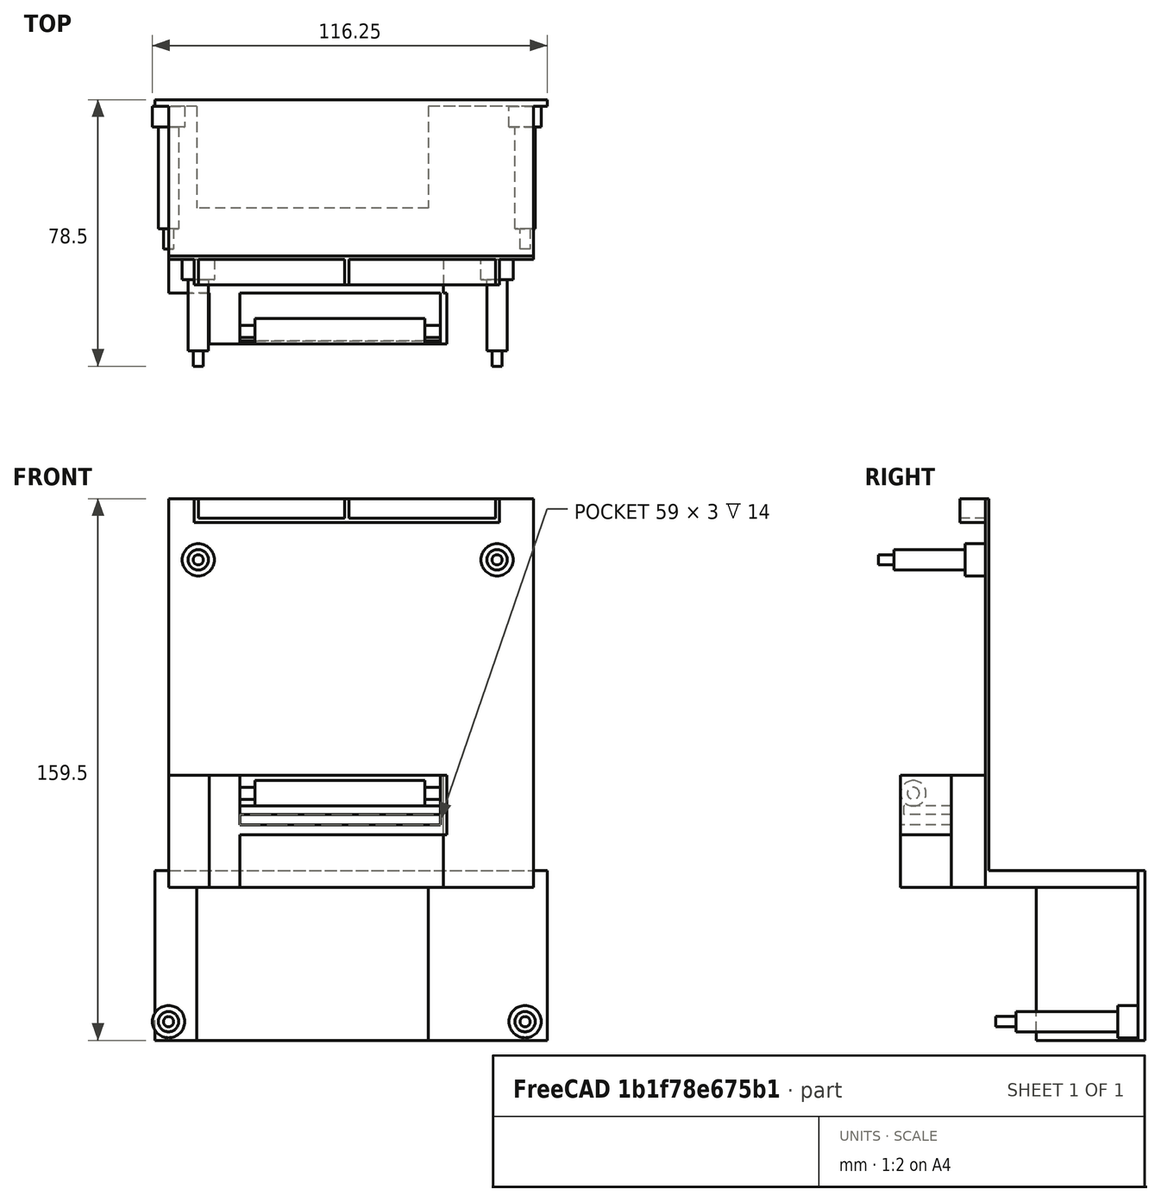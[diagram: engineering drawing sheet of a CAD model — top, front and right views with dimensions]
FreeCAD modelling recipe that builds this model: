
FCSTD DOCUMENT  (FreeCAD 1.0R39285 (Git))
Label: Modified-Printer-approximation
License: All rights reserved
LicenseURL: https://en.wikipedia.org/wiki/All_rights_reserved
objects: Sketcher::SketchObject×17, PartDesign::Pad×17, Part::Helix×2, App::Link×2, PartDesign::Body×1
note: 88 computed .brp shape members not serialized (recipe doc carries the construction recipe); baked Part::Feature solids carry a one-line shape summary decoded from their .brp

FEATURE [Sketcher::SketchObject] Sketch004
  ArcFitTolerance = 1e-06
  AttachmentSupport = -> [XZ_Plane002]
  FullyConstrained = true
  MakeInternals = false
  MapMode = 5
  Placement = pos=(0,0,0) rot=(1,0,0;1.5708rad)
  sketch-geometry (4):
    g0: LineSegment StartX=0 StartY=0 StartZ=0 EndX=0 EndY=-114.5 EndZ=0
    g1: LineSegment StartX=0 StartY=-114.5 StartZ=0 EndX=107.5 EndY=-114.5 EndZ=0
    g2: LineSegment StartX=107.5 StartY=-114.5 StartZ=0 EndX=107.5 EndY=0 EndZ=0
    g3: LineSegment StartX=107.5 StartY=0 StartZ=0 EndX=0 EndY=0 EndZ=0
  constraints (11):
    c: Coincident(g0,g1)
    c: Coincident(g1,g2)
    c: Coincident(g2,g3)
    c: Coincident(g3,g0)
    c: Vertical(g0)
    c: Vertical(g2)
    c: Horizontal(g1)
    c: Horizontal(g3)
    c: Distance(g0,g2) = 107.5
    c: Distance(g1,g3) = 114.5
    c: Coincident(g0,g-1)
FEATURE [PartDesign::Pad] Pad
  Direction = (0,-1,2e-16)
  Length = 1
  Length2 = 10
  Placement = pos=(0,0,0) rot=(1,0,0;1.5708rad)
  Profile = -> Sketch004
  ReferenceAxis = -> Sketch004 [N_Axis]
  Refine = true
  Reversed = true
  Suppressed = false
  Type = 0
FEATURE [Sketcher::SketchObject] Sketch
  ArcFitTolerance = 1e-06
  AttachmentSupport = -> [Pad]
  ExternalGeometry = -> [Pad]
  FullyConstrained = true
  MakeInternals = false
  MapMode = 5
  Placement = pos=(0,-1.27e-14,0) rot=(1,0,0;1.5708rad)
  sketch-geometry (15):
    g0: LineSegment StartX=97.5 StartY=0 StartZ=0 EndX=96.25 EndY=0 EndZ=0
    g1: LineSegment StartX=96.25 StartY=0 StartZ=0 EndX=96.25 EndY=-5.75 EndZ=0
    g2: LineSegment StartX=97.5 StartY=-7 StartZ=0 EndX=97.5 EndY=0 EndZ=0
    g3: LineSegment StartX=96.25 StartY=-5.75 StartZ=0 EndX=53.125 EndY=-5.75 EndZ=0
    g4: LineSegment StartX=7.5 StartY=-7 StartZ=0 EndX=97.5 EndY=-7 EndZ=0
    g5: LineSegment StartX=7.5 StartY=-7 StartZ=0 EndX=7.5 EndY=0 EndZ=0
    g6: LineSegment StartX=8.75 StartY=-5.75 StartZ=0 EndX=8.75 EndY=0 EndZ=0
    g7: LineSegment StartX=8.75 StartY=0 StartZ=0 EndX=7.5 EndY=0 EndZ=0
    g8: LineSegment StartX=53.125 StartY=-5.75 StartZ=0 EndX=53.125 EndY=0 EndZ=0
    g9: LineSegment StartX=53.125 StartY=0 StartZ=0 EndX=51.875 EndY=0 EndZ=0
    g10: LineSegment StartX=51.875 StartY=0 StartZ=0 EndX=51.875 EndY=-5.75 EndZ=0
    g11: LineSegment StartX=51.875 StartY=-5.75 StartZ=0 EndX=8.75 EndY=-5.75 EndZ=0
    g12: LineSegment [constr] StartX=53.125 StartY=-5.75 StartZ=0 EndX=53.125 EndY=-7 EndZ=0
    g13: LineSegment [constr] StartX=0 StartY=0 StartZ=0 EndX=7.5 EndY=0 EndZ=0
    g14: LineSegment [constr] StartX=97.5 StartY=0 StartZ=0 EndX=107.5 EndY=0 EndZ=0
  constraints (44):
    c: Coincident(g0,g1)
    c: Coincident(g2,g0)
    c: Horizontal(g0)
    c: Vertical(g1)
    c: Vertical(g2)
    c: Distance(g1,g2) = 1.25
    c: Distance(g0,g2) = 7
    c: PointOnObject(g0,g-1)
    c: Horizontal(g3)
    c: Horizontal(g4)
    c: Distance(g4,g4) = 90
    c: Coincident(g1,g3)
    c: Coincident(g2,g4)
    c: Coincident(g5,g4)
    c: PointOnObject(g5,g-1)
    c: Vertical(g5)
    c: Coincident(g6,g11)
    c: PointOnObject(g6,g-1)
    c: Vertical(g6)
    c: Coincident(g7,g6)
    c: Coincident(g7,g5)
    c: Equal(g7,g0)
    c: Coincident(g8,g9)
    c: Coincident(g9,g10)
    c: Horizontal(g9)
    c: Vertical(g8)
    c: Vertical(g10)
    c: PointOnObject(g8,g-1)
    c: Coincident(g10,g11)
    c: Coincident(g3,g8)
    c: Horizontal(g10,g3)
    c: Equal(g9,g7)
    c: Horizontal(g11)
    c: Vertical(g12)
    c: PointOnObject(g12,g4)
    c: Equal(g12,g9)
    c: Coincident(g3,g12)
    c: Equal(g11,g3)
    c: Coincident(g13,g-1)
    c: Coincident(g13,g5)
    c: DistanceX(g13,g13) = 7.5
    c: Coincident(g14,g0)
    c: Coincident(g14,g-3)
    c: DistanceX(g14,g14) = 10
FEATURE [PartDesign::Pad] Pad001
  BaseFeature = -> Pad
  Direction = (0,-1,2e-16)
  Length = 7.5
  Length2 = 10
  Placement = pos=(0,0,0) rot=(1,0,0;1.5708rad)
  Profile = -> Sketch
  ReferenceAxis = -> Sketch [N_Axis]
  Refine = true
  Suppressed = false
  Type = 0
FEATURE [Sketcher::SketchObject] Sketch005
  ArcFitTolerance = 1e-06
  AttachmentSupport = -> [Pad001]
  ExternalGeometry = -> [Pad001]
  FullyConstrained = true
  MakeInternals = false
  MapMode = 5
  Placement = pos=(0,-1.27e-14,0) rot=(1,0,0;1.5708rad)
  sketch-geometry (4):
    g0: Circle CenterX=8.75 CenterY=-18 CenterZ=0 NormalX=0 NormalY=0 NormalZ=1 AngleXU=0 Radius=4.75
    g1: Circle CenterX=96.75 CenterY=-18 CenterZ=0 NormalX=0 NormalY=0 NormalZ=1 AngleXU=0 Radius=4.75
    g2: LineSegment [constr] StartX=4 StartY=-18 StartZ=0 EndX=0 EndY=-18 EndZ=0
    g3: LineSegment [constr] StartX=101.5 StartY=-18 StartZ=0 EndX=107.5 EndY=-18 EndZ=0
  constraints (14):
    c: Equal(g0,g1)
    c: Horizontal(g1,g0)
    c: Diameter(g0) = 9.5
    c: PointOnObject(g2,g0)
    c: PointOnObject(g2,g-3)
    c: Horizontal(g2)
    c: Horizontal(g2,g0)
    c: PointOnObject(g3,g1)
    c: PointOnObject(g3,g-4)
    c: Horizontal(g3)
    c: Horizontal(g3,g1)
    c: DistanceX(g3,g3) = 6
    c: DistanceX(g2,g2) = 4
    c: DistanceY(g0,g-1) = 18
FEATURE [PartDesign::Pad] Pad002
  BaseFeature = -> Pad001
  Direction = (0,-1,2e-16)
  Length = 6
  Length2 = 10
  Placement = pos=(0,0,0) rot=(1,0,0;1.5708rad)
  Profile = -> Sketch005
  ReferenceAxis = -> Sketch005 [N_Axis]
  Refine = true
  Suppressed = false
  Type = 0
FEATURE [Sketcher::SketchObject] Sketch006
  ArcFitTolerance = 1e-06
  AttachmentSupport = -> [Pad002]
  ExternalGeometry = -> [Pad002]
  FullyConstrained = true
  MakeInternals = false
  MapMode = 5
  Placement = pos=(0,-6,0) rot=(1,0,0;1.5708rad)
  sketch-geometry (2):
    g0: Circle CenterX=8.75 CenterY=-18 CenterZ=0 NormalX=0 NormalY=0 NormalZ=1 AngleXU=0 Radius=3
    g1: Circle CenterX=96.75 CenterY=-18 CenterZ=0 NormalX=0 NormalY=0 NormalZ=1 AngleXU=0 Radius=3
  constraints (4):
    c: Coincident(g0,g-3)
    c: Coincident(g1,g-4)
    c: Equal(g0,g1)
    c: Diameter(g0) = 6
FEATURE [PartDesign::Pad] Pad003
  BaseFeature = -> Pad002
  Direction = (0,-1,2e-16)
  Length = 21
  Length2 = 10
  Placement = pos=(0,0,0) rot=(1,0,0;1.5708rad)
  Profile = -> Sketch006
  ReferenceAxis = -> Sketch006 [N_Axis]
  Refine = true
  Suppressed = false
  Type = 0
FEATURE [Sketcher::SketchObject] Sketch007
  ArcFitTolerance = 1e-06
  AttachmentSupport = -> [Pad003]
  ExternalGeometry = -> [Pad003]
  FullyConstrained = true
  MakeInternals = false
  MapMode = 5
  Placement = pos=(0,-27,0) rot=(1,0,0;1.5708rad)
  sketch-geometry (2):
    g0: Circle CenterX=8.75 CenterY=-18 CenterZ=0 NormalX=0 NormalY=0 NormalZ=1 AngleXU=0 Radius=1.5
    g1: Circle CenterX=96.75 CenterY=-18 CenterZ=0 NormalX=0 NormalY=0 NormalZ=1 AngleXU=0 Radius=1.5
  constraints (4):
    c: Diameter(g0) = 3
    c: Coincident(g0,g-3)
    c: Coincident(g1,g-4)
    c: Equal(g1,g0)
FEATURE [PartDesign::Pad] Pad004
  BaseFeature = -> Pad003
  Direction = (0,-1,2e-16)
  Length = 4.5
  Length2 = 10
  Placement = pos=(0,0,0) rot=(1,0,0;1.5708rad)
  Profile = -> Sketch007
  ReferenceAxis = -> Sketch007 [N_Axis]
  Refine = true
  Suppressed = false
  Type = 0
FEATURE [Part::Helix] Helix002
  Angle = 0
  AttacherType = Attacher::AttachEngine3D
  Height = 4.5
  Length = 42.6496
  LocalCoord = 0
  Pitch = 1
  Placement = pos=(8.75,-27,-18) rot=(1,0,0;1.5708rad)
  Radius = 1.5
  SegmentLength = 0
  Style = 1
FEATURE [App::Link] Link  label="Helix003"
  LinkPlacement = pos=(96.75,-27,-18) rot=(1,0,0;1.5708rad)
  LinkedObject = -> Helix002
  Placement = pos=(96.75,-27,-18) rot=(1,0,0;1.5708rad)
FEATURE [Sketcher::SketchObject] Sketch008
  ArcFitTolerance = 1e-06
  AttachmentSupport = -> [Pad004]
  ExternalGeometry = -> [Pad004]
  FullyConstrained = true
  MakeInternals = false
  MapMode = 5
  Placement = pos=(0,-1.27e-14,0) rot=(1,0,0;1.5708rad)
  sketch-geometry (4):
    g0: LineSegment StartX=0 StartY=-114.5 StartZ=0 EndX=81 EndY=-114.5 EndZ=0
    g1: LineSegment StartX=81 StartY=-114.5 StartZ=0 EndX=81 EndY=-81.5 EndZ=0
    g2: LineSegment StartX=81 StartY=-81.5 StartZ=0 EndX=0 EndY=-81.5 EndZ=0
    g3: LineSegment StartX=0 StartY=-81.5 StartZ=0 EndX=0 EndY=-114.5 EndZ=0
  constraints (11):
    c: Coincident(g0,g1)
    c: Coincident(g1,g2)
    c: Coincident(g2,g3)
    c: Coincident(g3,g0)
    c: Horizontal(g0)
    c: Horizontal(g2)
    c: Vertical(g1)
    c: Vertical(g3)
    c: Distance(g1,g3) = 81
    c: Distance(g0,g2) = 33
    c: Coincident(g0,g-3)
FEATURE [PartDesign::Pad] Pad005
  BaseFeature = -> Pad004
  Direction = (0,-1,2e-16)
  Length = 10
  Length2 = 10
  Placement = pos=(0,0,0) rot=(1,0,0;1.5708rad)
  Profile = -> Sketch008
  ReferenceAxis = -> Sketch008 [N_Axis]
  Refine = true
  Suppressed = false
  Type = 0
FEATURE [Sketcher::SketchObject] Sketch009
  ArcFitTolerance = 1e-06
  AttachmentSupport = -> [Pad005]
  ExternalGeometry = -> [Pad005]
  FullyConstrained = true
  MakeInternals = false
  MapMode = 5
  Placement = pos=(0,-10,0) rot=(1,0,0;1.5708rad)
  sketch-geometry (11):
    g0: LineSegment StartX=21 StartY=-81.5 StartZ=0 EndX=12 EndY=-81.5 EndZ=0
    g1: LineSegment StartX=12 StartY=-81.5 StartZ=0 EndX=12 EndY=-114.5 EndZ=0
    g2: LineSegment StartX=12 StartY=-114.5 StartZ=0 EndX=21 EndY=-114.5 EndZ=0
    g3: LineSegment StartX=21 StartY=-114.5 StartZ=0 EndX=21 EndY=-99 EndZ=0
    g4: LineSegment StartX=82 StartY=-99 StartZ=0 EndX=82 EndY=-81.5 EndZ=0
    g5: LineSegment StartX=80 StartY=-96 StartZ=0 EndX=21 EndY=-96 EndZ=0
    g6: LineSegment StartX=21 StartY=-99 StartZ=0 EndX=82 EndY=-99 EndZ=0
    g7: LineSegment StartX=21 StartY=-96 StartZ=0 EndX=21 EndY=-81.5 EndZ=0
    g8: LineSegment StartX=80 StartY=-81.5 StartZ=0 EndX=80 EndY=-96 EndZ=0
    g9: LineSegment StartX=80 StartY=-81.5 StartZ=0 EndX=82 EndY=-81.5 EndZ=0
    g10: LineSegment [constr] StartX=21 StartY=-96 StartZ=0 EndX=21 EndY=-99 EndZ=0
  constraints (32):
    c: Coincident(g0,g1)
    c: Coincident(g1,g2)
    c: Coincident(g2,g3)
    c: Coincident(g7,g0)
    c: Horizontal(g0)
    c: Horizontal(g2)
    c: Vertical(g1)
    c: Vertical(g3)
    c: DistanceX(g0,g0) = 9
    c: PointOnObject(g2,g-3)
    c: Vertical(g4)
    c: DistanceY(g4,g4) = 17.5
    c: Horizontal(g5)
    c: Horizontal(g6)
    c: PointOnObject(g5,g7)
    c: PointOnObject(g7,g5)
    c: Vertical(g7)
    c: Coincident(g3,g6)
    c: Vertical(g3,g5)
    c: DistanceX(g-3,g1) = 12
    c: Vertical(g8)
    c: Coincident(g9,g8)
    c: Coincident(g9,g4)
    c: Horizontal(g9)
    c: DistanceX(g9,g9) = 2
    c: Symmetric(g8,g4,g-4)
    c: PointOnObject(g0,g-5)
    c: Coincident(g5,g8)
    c: Coincident(g10,g5)
    c: Coincident(g10,g3)
    c: DistanceY(g10,g10) = 3
    c: Coincident(g4,g6)
FEATURE [PartDesign::Pad] Pad006
  BaseFeature = -> Pad005
  Direction = (0,-1,2e-16)
  Length = 15
  Length2 = 10
  Placement = pos=(0,0,0) rot=(1,0,0;1.5708rad)
  Profile = -> Sketch009
  ReferenceAxis = -> Sketch009 [N_Axis]
  Refine = true
  Suppressed = false
  Type = 0
FEATURE [Sketcher::SketchObject] Sketch010
  ArcFitTolerance = 1e-06
  AttachmentSupport = -> [Pad006]
  ExternalGeometry = -> [Pad006]
  FullyConstrained = true
  MakeInternals = false
  MapMode = 5
  Placement = pos=(0,-10,0) rot=(1,0,0;1.5708rad)
  sketch-geometry (4):
    g0: LineSegment StartX=21 StartY=-90.5 StartZ=0 EndX=21 EndY=-93 EndZ=0
    g1: LineSegment StartX=21 StartY=-93 StartZ=0 EndX=80 EndY=-93 EndZ=0
    g2: LineSegment StartX=80 StartY=-93 StartZ=0 EndX=80 EndY=-90.5 EndZ=0
    g3: LineSegment StartX=80 StartY=-90.5 StartZ=0 EndX=21 EndY=-90.5 EndZ=0
  constraints (12):
    c: Coincident(g0,g1)
    c: Coincident(g1,g2)
    c: Coincident(g2,g3)
    c: Coincident(g3,g0)
    c: Vertical(g0)
    c: Vertical(g2)
    c: Horizontal(g1)
    c: Horizontal(g3)
    c: PointOnObject(g0,g-4)
    c: PointOnObject(g1,g-5)
    c: DistanceY(g0,g0) = 2.5
    c: DistanceY(g-4,g0) = 3
FEATURE [PartDesign::Pad] Pad007
  BaseFeature = -> Pad006
  Direction = (0,-1,2e-16)
  Length = 14
  Length2 = 10
  Placement = pos=(0,0,0) rot=(1,0,0;1.5708rad)
  Profile = -> Sketch010
  ReferenceAxis = -> Sketch010 [N_Axis]
  Refine = true
  Suppressed = false
  Type = 0
FEATURE [Sketcher::SketchObject] Sketch011
  ArcFitTolerance = 1e-06
  AttachmentSupport = -> [Pad007]
  ExternalGeometry = -> [Pad007]
  FullyConstrained = true
  MakeInternals = false
  MapMode = 5
  Placement = pos=(21,0,0) rot=(0.707107,0,0.707107;3.14159rad)
  sketch-geometry (4):
    g0: Circle CenterX=-86.75 CenterY=21.25 CenterZ=0 NormalX=0 NormalY=0 NormalZ=1 AngleXU=0 Radius=1.75
    g1: Circle [constr] CenterX=-86.75 CenterY=21.25 CenterZ=0 NormalX=0 NormalY=0 NormalZ=1 AngleXU=0 Radius=3.75
    g2: GeomPoint [constr] X=-90.5 Y=21.25 Z=0
    g3: GeomPoint [constr] X=-86.75 Y=25 Z=0
  constraints (9):
    c: Diameter(g0) = 3.5
    c: Diameter(g1) = 7.5
    c: Coincident(g1,g0)
    c: PointOnObject(g2,g1)
    c: Horizontal(g2,g0)
    c: PointOnObject(g2,g-3)
    c: PointOnObject(g3,g1)
    c: Vertical(g3,g0)
    c: PointOnObject(g3,g-5)
FEATURE [PartDesign::Pad] Pad008
  BaseFeature = -> Pad007
  Direction = (1,0,-2e-16)
  Length = 4.5
  Length2 = 10
  Placement = pos=(0,0,0) rot=(1,0,0;1.5708rad)
  Profile = -> Sketch011
  ReferenceAxis = -> Sketch011 [N_Axis]
  Refine = true
  Suppressed = false
  Type = 0
FEATURE [Sketcher::SketchObject] Sketch012
  ArcFitTolerance = 1e-06
  AttachmentSupport = -> [Pad008]
  ExternalGeometry = -> [Pad008]
  FullyConstrained = true
  MakeInternals = false
  MapMode = 5
  Placement = pos=(25.5,0,0) rot=(0.707107,0,0.707107;3.14159rad)
  sketch-geometry (1):
    g0: Circle CenterX=-86.75 CenterY=21.25 CenterZ=0 NormalX=0 NormalY=0 NormalZ=1 AngleXU=0 Radius=3.75
  constraints (2):
    c: Coincident(g0,g-3)
    c: Diameter(g0) = 7.5
FEATURE [PartDesign::Pad] Pad009
  BaseFeature = -> Pad008
  Direction = (1,0,-2e-16)
  Length = 50
  Length2 = 10
  Placement = pos=(0,0,0) rot=(1,0,0;1.5708rad)
  Profile = -> Sketch012
  ReferenceAxis = -> Sketch012 [N_Axis]
  Refine = true
  Suppressed = false
  Type = 0
FEATURE [Sketcher::SketchObject] Sketch013
  ArcFitTolerance = 1e-06
  AttachmentSupport = -> [Pad009]
  ExternalGeometry = -> [Pad009]
  FullyConstrained = true
  MakeInternals = false
  MapMode = 5
  Placement = pos=(75.5,0,-4.77e-14) rot=(0.707107,0,0.707107;3.14159rad)
  sketch-geometry (1):
    g0: Circle CenterX=-86.75 CenterY=21.25 CenterZ=0 NormalX=0 NormalY=0 NormalZ=1 AngleXU=0 Radius=1.75
  constraints (2):
    c: Coincident(g0,g-3)
    c: Diameter(g0) = 3.5
FEATURE [PartDesign::Pad] Pad010
  BaseFeature = -> Pad009
  Direction = (1,0,-2e-16)
  Length = 4.5
  Length2 = 10
  Placement = pos=(0,0,0) rot=(1,0,0;1.5708rad)
  Profile = -> Sketch013
  ReferenceAxis = -> Sketch013 [N_Axis]
  Refine = true
  Suppressed = false
  Type = 0
FEATURE [Sketcher::SketchObject] Sketch014
  ArcFitTolerance = 1e-06
  AttachmentSupport = -> [Pad010]
  ExternalGeometry = -> [Pad010]
  FullyConstrained = true
  MakeInternals = false
  MapMode = 5
  Placement = pos=(0,1,0) rot=(-1,0,0;1.5708rad)
  sketch-geometry (4):
    g0: LineSegment StartX=0 StartY=114.5 StartZ=0 EndX=0 EndY=109.5 EndZ=0
    g1: LineSegment StartX=0 StartY=109.5 StartZ=0 EndX=107.5 EndY=109.5 EndZ=0
    g2: LineSegment StartX=107.5 StartY=109.5 StartZ=0 EndX=107.5 EndY=114.5 EndZ=0
    g3: LineSegment StartX=107.5 StartY=114.5 StartZ=0 EndX=0 EndY=114.5 EndZ=0
  constraints (10):
    c: Coincident(g0,g1)
    c: Coincident(g1,g2)
    c: Coincident(g2,g3)
    c: Coincident(g3,g0)
    c: Vertical(g0)
    c: Vertical(g2)
    c: Horizontal(g1)
    c: Coincident(g0,g-3)
    c: Coincident(g2,g-3)
    c: DistanceY(g2,g2) = 5
FEATURE [PartDesign::Pad] Pad011
  BaseFeature = -> Pad010
  Direction = (0,1,2e-16)
  Length = 44
  Length2 = 10
  Placement = pos=(0,0,0) rot=(1,0,0;1.5708rad)
  Profile = -> Sketch014
  ReferenceAxis = -> Sketch014 [N_Axis]
  Refine = true
  Suppressed = false
  Type = 0
FEATURE [Sketcher::SketchObject] Sketch015
  ArcFitTolerance = 1e-06
  AttachmentSupport = -> [Pad011]
  ExternalGeometry = -> [Pad011]
  FullyConstrained = true
  MakeInternals = false
  MapMode = 5
  Placement = pos=(0,45,1e-14) rot=(-1,0,0;1.5708rad)
  sketch-geometry (4):
    g0: LineSegment StartX=-4 StartY=109.5 StartZ=0 EndX=111.5 EndY=109.5 EndZ=0
    g1: LineSegment StartX=111.5 StartY=109.5 StartZ=0 EndX=111.5 EndY=159.5 EndZ=0
    g2: LineSegment StartX=111.5 StartY=159.5 StartZ=0 EndX=-4 EndY=159.5 EndZ=0
    g3: LineSegment StartX=-4 StartY=159.5 StartZ=0 EndX=-4 EndY=109.5 EndZ=0
  constraints (12):
    c: Coincident(g0,g1)
    c: Coincident(g1,g2)
    c: Coincident(g2,g3)
    c: Coincident(g3,g0)
    c: Horizontal(g0)
    c: Horizontal(g2)
    c: Vertical(g1)
    c: Vertical(g3)
    c: DistanceY(g-3,g2) = 45
    c: DistanceX(g0,g-4) = 4
    c: DistanceX(g-4,g0) = 4
    c: Horizontal(g0,g-4)
FEATURE [PartDesign::Pad] Pad012
  BaseFeature = -> Pad011
  Direction = (0,1,2e-16)
  Length = 2
  Length2 = 10
  Placement = pos=(0,0,0) rot=(1,0,0;1.5708rad)
  Profile = -> Sketch015
  ReferenceAxis = -> Sketch015 [N_Axis]
  Refine = true
  Suppressed = false
  Type = 0
FEATURE [Sketcher::SketchObject] Sketch016
  ArcFitTolerance = 1e-06
  AttachmentSupport = -> [Pad012]
  ExternalGeometry = -> [Pad012]
  FullyConstrained = true
  MakeInternals = false
  MapMode = 5
  Placement = pos=(0,45,1.28e-14) rot=(1,0,0;1.5708rad)
  sketch-geometry (2):
    g0: Circle CenterX=0 CenterY=-154 CenterZ=0 NormalX=0 NormalY=0 NormalZ=1 AngleXU=0 Radius=4.75
    g1: Circle CenterX=105 CenterY=-154 CenterZ=0 NormalX=0 NormalY=0 NormalZ=1 AngleXU=0 Radius=4.75
  constraints (6):
    c: Equal(g1,g0)
    c: Horizontal(g0,g1)
    c: Diameter(g1) = 9.5
    c: DistanceY(g0,g-9) = 39.5
    c: DistanceX(g0,g1) = 105
    c: Vertical(g-9,g0)
FEATURE [PartDesign::Pad] Pad013
  BaseFeature = -> Pad012
  Direction = (0,-1,2e-16)
  Length = 6
  Length2 = 10
  Placement = pos=(0,0,0) rot=(1,0,0;1.5708rad)
  Profile = -> Sketch016
  ReferenceAxis = -> Sketch016 [N_Axis]
  Refine = true
  Suppressed = false
  Type = 0
FEATURE [Sketcher::SketchObject] Sketch017
  ArcFitTolerance = 1e-06
  AttachmentSupport = -> [Pad013]
  ExternalGeometry = -> [Pad013]
  FullyConstrained = true
  MakeInternals = false
  MapMode = 5
  Placement = pos=(0,39,0) rot=(1,0,0;1.5708rad)
  sketch-geometry (2):
    g0: Circle CenterX=105 CenterY=-154 CenterZ=0 NormalX=0 NormalY=0 NormalZ=1 AngleXU=0 Radius=3
    g1: Circle CenterX=0 CenterY=-154 CenterZ=0 NormalX=0 NormalY=0 NormalZ=1 AngleXU=0 Radius=3
  constraints (4):
    c: Diameter(g0) = 6
    c: Coincident(g0,g-4)
    c: Coincident(g1,g-3)
    c: Equal(g1,g0)
FEATURE [PartDesign::Pad] Pad014
  BaseFeature = -> Pad013
  Direction = (0,-1,2e-16)
  Length = 30
  Length2 = 10
  Placement = pos=(0,0,0) rot=(1,0,0;1.5708rad)
  Profile = -> Sketch017
  ReferenceAxis = -> Sketch017 [N_Axis]
  Refine = true
  Suppressed = false
  Type = 0
FEATURE [Sketcher::SketchObject] Sketch018
  ArcFitTolerance = 1e-06
  AttachmentSupport = -> [Pad014]
  ExternalGeometry = -> [Pad014]
  FullyConstrained = true
  MakeInternals = false
  MapMode = 5
  Placement = pos=(0,9,0) rot=(1,0,0;1.5708rad)
  sketch-geometry (2):
    g0: Circle CenterX=0 CenterY=-154 CenterZ=0 NormalX=0 NormalY=0 NormalZ=1 AngleXU=0 Radius=1.5
    g1: Circle CenterX=105 CenterY=-154 CenterZ=0 NormalX=0 NormalY=0 NormalZ=1 AngleXU=0 Radius=1.5
  constraints (4):
    c: Diameter(g0) = 3
    c: Coincident(g0,g-4)
    c: Coincident(g1,g-3)
    c: Equal(g1,g0)
FEATURE [PartDesign::Pad] Pad015
  BaseFeature = -> Pad014
  Direction = (0,-1,2e-16)
  Length = 6
  Length2 = 10
  Placement = pos=(0,0,0) rot=(1,0,0;1.5708rad)
  Profile = -> Sketch018
  ReferenceAxis = -> Sketch018 [N_Axis]
  Refine = true
  Suppressed = false
  Type = 0
FEATURE [Sketcher::SketchObject] Sketch019
  ArcFitTolerance = 1e-06
  AttachmentSupport = -> [Pad015]
  ExternalGeometry = -> [Pad015]
  FullyConstrained = true
  MakeInternals = false
  MapMode = 5
  Placement = pos=(0,45,1.28e-14) rot=(1,0,0;1.5708rad)
  sketch-geometry (4):
    g0: LineSegment StartX=8.25 StartY=-159.5 StartZ=0 EndX=76.5 EndY=-159.5 EndZ=0
    g1: LineSegment StartX=76.5 StartY=-159.5 StartZ=0 EndX=76.5 EndY=-114.5 EndZ=0
    g2: LineSegment StartX=76.5 StartY=-114.5 StartZ=0 EndX=8.25 EndY=-114.5 EndZ=0
    g3: LineSegment StartX=8.25 StartY=-114.5 StartZ=0 EndX=8.25 EndY=-159.5 EndZ=0
  constraints (12):
    c: Coincident(g0,g1)
    c: Coincident(g1,g2)
    c: Coincident(g2,g3)
    c: Coincident(g3,g0)
    c: Horizontal(g0)
    c: Horizontal(g2)
    c: Vertical(g1)
    c: Vertical(g3)
    c: PointOnObject(g0,g-3)
    c: PointOnObject(g1,g-4)
    c: DistanceX(g-5,g0) = 3.5
    c: DistanceX(g1,g-6) = 4.5
FEATURE [PartDesign::Pad] Pad016
  BaseFeature = -> Pad015
  Direction = (0,-1,2e-16)
  Length = 30
  Length2 = 10
  Placement = pos=(0,0,0) rot=(1,0,0;1.5708rad)
  Profile = -> Sketch019
  ReferenceAxis = -> Sketch019 [N_Axis]
  Refine = true
  Suppressed = false
  Type = 0
FEATURE [PartDesign::Body] Body002  label="Körper002"
  AllowCompound = false
  Group = -> [Sketch004,Pad,Sketch,Pad001,Sketch005,Pad002,Sketch006,Pad003,Sketch007,Pad004,Sketch008,Pad005,Sketch009,Pad006,Sketch010,Pad007,Sketch011,Pad008,Sketch012,Pad009,Sketch013,Pad010,Sketch014,Pad011,Sketch015,Pad012,Sketch016,Pad013,Sketch017,Pad014,Sketch018,Pad015,Sketch019,Pad016]
  Origin = -> Origin002
  Tip = -> Pad016
FEATURE [Part::Helix] Helix003  label="Helix004"
  Angle = 0
  AttacherType = Attacher::AttachEngine3D
  Height = 4.5
  Length = 42.6496
  LocalCoord = 0
  Pitch = 1
  Placement = pos=(0,7.5,-154) rot=(1,0,0;1.5708rad)
  Radius = 1.5
  SegmentLength = 0
  Style = 1
FEATURE [App::Link] Link001  label="Helix005"
  LinkPlacement = pos=(105,7.49999,-154) rot=(1,0,0;1.5708rad)
  LinkedObject = -> Helix003
  Placement = pos=(105,7.49999,-154) rot=(1,0,0;1.5708rad)
